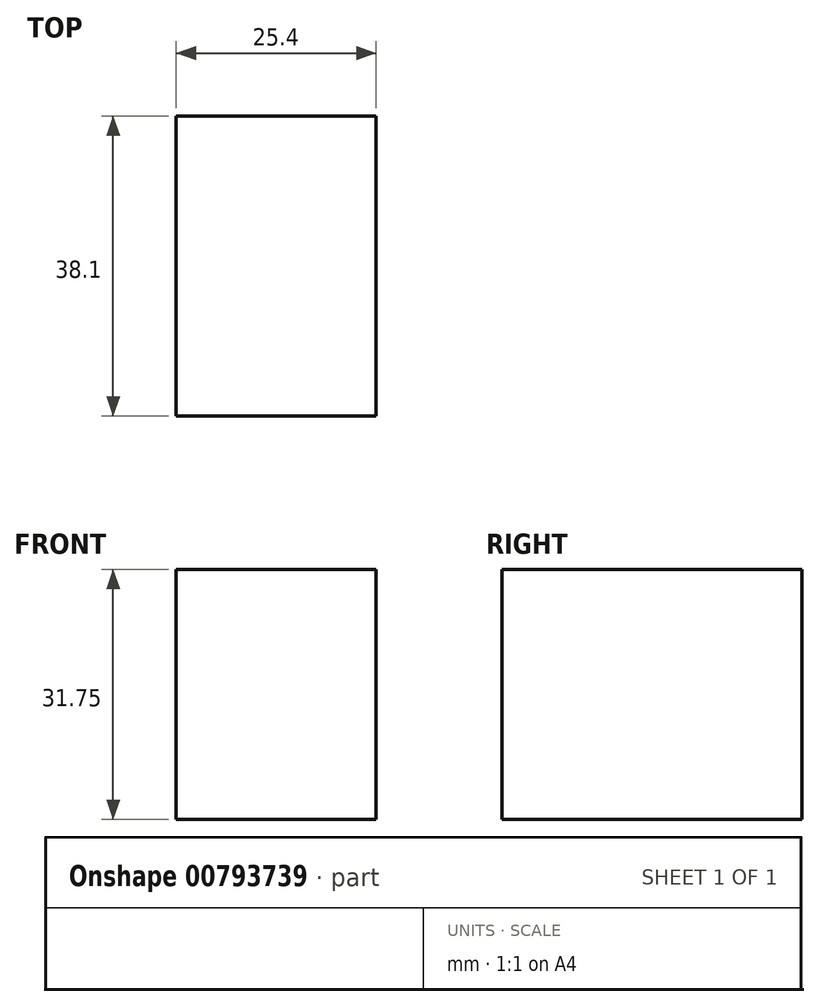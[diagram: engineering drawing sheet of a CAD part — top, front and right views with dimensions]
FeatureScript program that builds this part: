
annotation { "Feature Type Name" : "Feature", "Feature Type Description" : "" }
export const myFeature = defineFeature(function(context is Context, id is Id, definition is map)
    precondition{}
    {
        {
            var Q0;
            Q0=qCreatedBy(makeId("Front.planeOp"),FACE);
            var sketch = newSketch(context, id + "F0", { "sketchPlane" : qUnion([Q0])});
            skLineSegment(sketch, "E0", {"start": v(0, 0) * mm, "end": v(25.4, 0) * mm});
            skLineSegment(sketch, "E1", {"start": v(25.4, 0) * mm, "end": v(25.4, 31.75) * mm});
            skLineSegment(sketch, "E2", {"start": v(25.4, 31.75) * mm, "end": v(0, 31.75) * mm});
            skLineSegment(sketch, "E3", {"start": v(0, 31.75) * mm, "end": v(0, 0) * mm});
            skSolve(sketch);
        }
        {
            var Q0;
            Q0=makeQuery(id+"F0.imprint","IMPRINT",FACE,{"disambiguationData":[TD([[makeQuery(id+"F0.imprint","IMPRINT",EDGE,{"derivedFrom":sQuery(id+"F0.wireOp",EDGE,"E0")}),1.0]])]});
            extrude(context, id + "F1", {"entities" : qUnion([Q0]), "depth" : 38.1 * mm, "offsetDistance" : 25.4 * mm});
        }
    });
